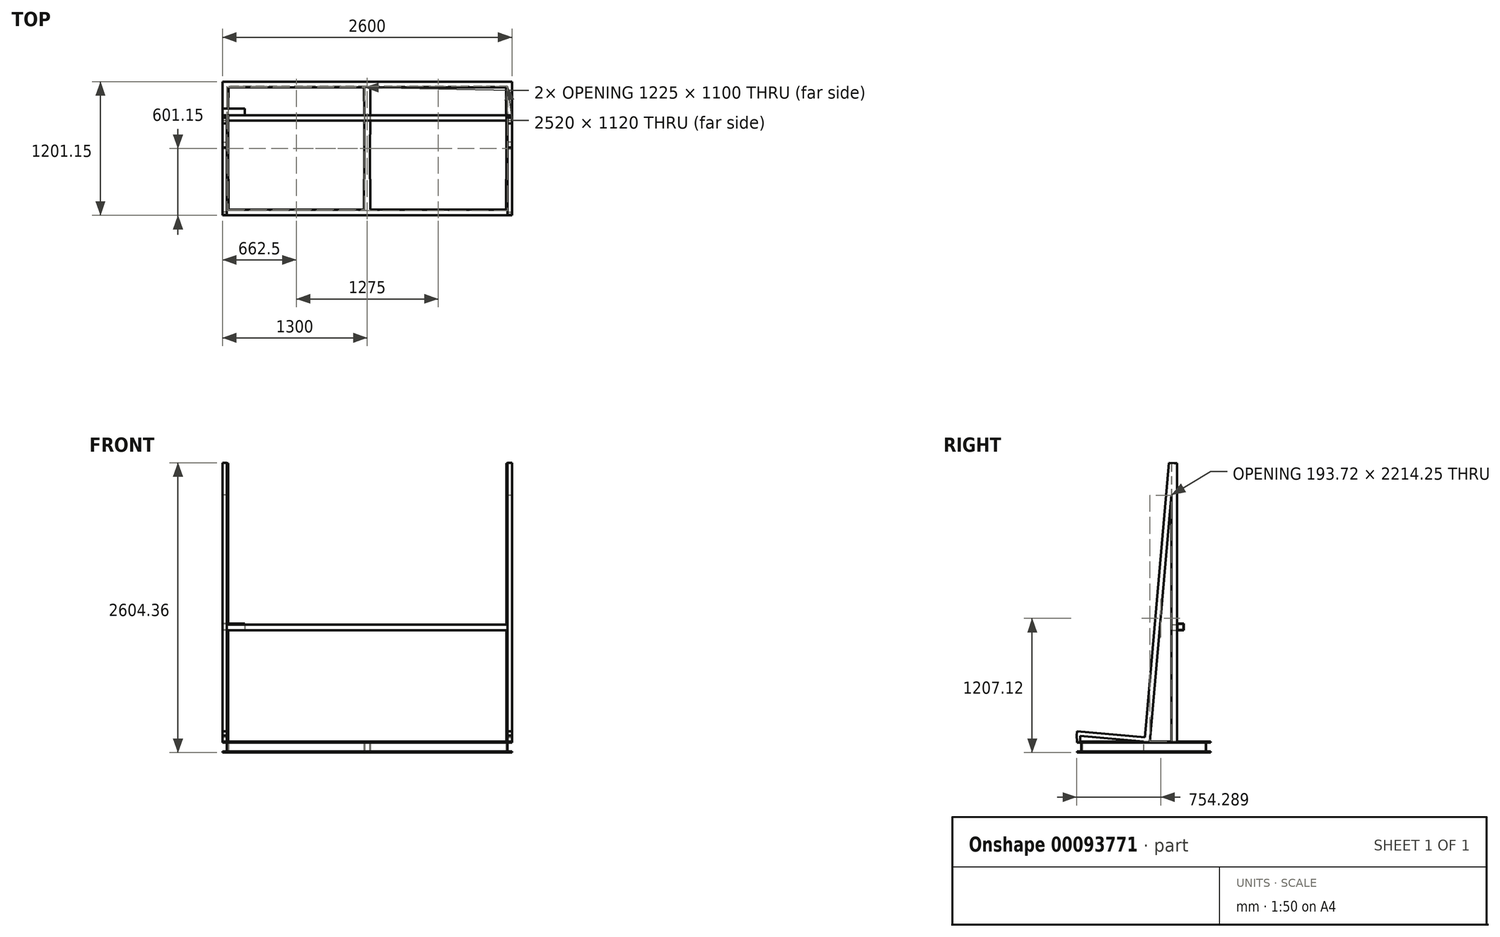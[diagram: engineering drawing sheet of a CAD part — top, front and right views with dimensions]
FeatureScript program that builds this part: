
annotation { "Feature Type Name" : "Feature", "Feature Type Description" : "" }
export const myFeature = defineFeature(function(context is Context, id is Id, definition is map)
    precondition{}
    {
        {
            var Q0;
            Q0=qCreatedBy(makeId("Top.planeOp"),FACE);
            var sketch = newSketch(context, id + "F0", { "sketchPlane" : qUnion([Q0])});
            skLineSegment(sketch, "E0.rect.bottom", {"start": v(1300, 600) * mm, "end": v(-1300, 600) * mm});
            skLineSegment(sketch, "E0.rect.top", {"start": v(1300, -600) * mm, "end": v(-1300, -600) * mm});
            skLineSegment(sketch, "E0.rect.left", {"start": v(1300, 600) * mm, "end": v(1300, -600) * mm});
            skLineSegment(sketch, "E0.rect.right", {"start": v(-1300, 600) * mm, "end": v(-1300, -600) * mm});
            skPoint(sketch, "E0.rect.middle", {"position": v(0, 0) * mm});
            skLineSegment(sketch, "E1.rect.bottom", {"start": v(1246.86, 550) * mm, "end": v(21.86, 550) * mm});
            skLineSegment(sketch, "E1.rect.top", {"start": v(1253.14, -550) * mm, "end": v(28.14, -550) * mm});
            skLineSegment(sketch, "E1.rect.left", {"start": v(1246.86, 550) * mm, "end": v(1253.14, -550) * mm});
            skLineSegment(sketch, "E1.rect.right", {"start": v(-1253.14, 550) * mm, "end": v(-1246.86, -550) * mm});
            skLineSegment(sketch, "E2.rect.left", {"start": v(21.86, 550) * mm, "end": v(28.14, -550) * mm});
            skLineSegment(sketch, "E2.rect.right", {"start": v(-28.14, 550) * mm, "end": v(-21.86, -550) * mm});
            skLineSegment(sketch, "E3.trimOffspring", {"start": v(-28.14, 550) * mm, "end": v(-1253.14, 550) * mm});
            skLineSegment(sketch, "E4.trimOffspring", {"start": v(-21.86, -550) * mm, "end": v(-1246.86, -550) * mm});
            skSolve(sketch);
        }
        {
            var Q0;
            Q0=makeQuery(id+"F0.imprint","IMPRINT",FACE,{"disambiguationData":[TD([[makeQuery(id+"F0.imprint","IMPRINT",EDGE,{"derivedFrom":sQuery(id+"F0.wireOp",EDGE,"E0.rect.bottom")}),1.0]])]});
            extrude(context, id + "F1", {"entities" : qUnion([Q0]), "depth" : 100 * mm});
        }
        {
            var Q0;
            Q0=makeQuery(id+"F1.opExtrude","SWEPT_FACE",FACE,{"disambiguationData":[OSD([sQuery(id+"F0.wireOp",EDGE,"E0.rect.right")])]});
            var sketch = newSketch(context, id + "F2", { "sketchPlane" : qUnion([Q0])});
            skLineSegment(sketch, "E5.bottom", {"start": v(-600, 90) * mm, "end": v(-560, 90) * mm});
            skLineSegment(sketch, "E5.top", {"start": v(-600, 10) * mm, "end": v(-560, 10) * mm});
            skLineSegment(sketch, "E5.left", {"start": v(-600, 90) * mm, "end": v(-600, 10) * mm});
            skLineSegment(sketch, "E5.right", {"start": v(-560, 90) * mm, "end": v(-560, 10) * mm});
            skLineSegment(sketch, "E6.bottom", {"start": v(600, 90) * mm, "end": v(560, 90) * mm});
            skLineSegment(sketch, "E6.top", {"start": v(600, 10) * mm, "end": v(560, 10) * mm});
            skLineSegment(sketch, "E6.left", {"start": v(600, 90) * mm, "end": v(600, 10) * mm});
            skLineSegment(sketch, "E6.right", {"start": v(560, 90) * mm, "end": v(560, 10) * mm});
            skSolve(sketch);
        }
        {
            var Q0;
            Q0=makeQuery(id+"F2.imprint","IMPRINT",FACE,{"disambiguationData":[TD([[makeQuery(id+"F2.imprint","IMPRINT",EDGE,{"derivedFrom":sQuery(id+"F2.wireOp",EDGE,"E5.bottom")}),-1.0]])]});
            var Q1;
            Q1=makeQuery(id+"F2.imprint","IMPRINT",FACE,{"disambiguationData":[TD([[makeQuery(id+"F2.imprint","IMPRINT",EDGE,{"derivedFrom":sQuery(id+"F2.wireOp",EDGE,"E6.bottom")}),1.0]])]});
            extrude(context, id + "F3", {"entities" : qUnion([Q0, Q1]), "operationType" : NewBodyOperationType.REMOVE, "endBound" : BoundingType.THROUGH_ALL, "oppositeDirection" : true, "depth" : 25 * mm});
        }
        {
            var Q0;
            Q0=makeQuery(id+"F3.boolean.opBoolean","COPY",FACE,{"derivedFrom":makeQuery(id+"F3.opExtrude","SWEPT_FACE",FACE,{"disambiguationData":[OSD([sQuery(id+"F2.wireOp",EDGE,"E6.right")])]})});
            var sketch = newSketch(context, id + "F4", { "sketchPlane" : qUnion([Q0])});
            skLineSegment(sketch, "E7.bottom", {"start": v(1300, 90) * mm, "end": v(1260, 90) * mm});
            skLineSegment(sketch, "E7.top", {"start": v(1300, 10) * mm, "end": v(1260, 10) * mm});
            skLineSegment(sketch, "E7.left", {"start": v(1300, 90) * mm, "end": v(1300, 10) * mm});
            skLineSegment(sketch, "E7.right", {"start": v(1260, 90) * mm, "end": v(1260, 10) * mm});
            skLineSegment(sketch, "E8.bottom", {"start": v(-1300, 90) * mm, "end": v(-1260, 90) * mm});
            skLineSegment(sketch, "E8.top", {"start": v(-1300, 10) * mm, "end": v(-1260, 10) * mm});
            skLineSegment(sketch, "E8.left", {"start": v(-1300, 90) * mm, "end": v(-1300, 10) * mm});
            skLineSegment(sketch, "E8.right", {"start": v(-1260, 90) * mm, "end": v(-1260, 10) * mm});
            skSolve(sketch);
        }
        {
            var Q0;
            Q0=makeQuery(id+"F4.imprint","IMPRINT",FACE,{"disambiguationData":[TD([[makeQuery(id+"F4.imprint","IMPRINT",EDGE,{"derivedFrom":sQuery(id+"F4.wireOp",EDGE,"E7.bottom")}),1.0]])]});
            var Q1;
            Q1=makeQuery(id+"F4.imprint","IMPRINT",FACE,{"disambiguationData":[TD([[makeQuery(id+"F4.imprint","IMPRINT",EDGE,{"derivedFrom":sQuery(id+"F4.wireOp",EDGE,"E8.bottom")}),1.0]])]});
            extrude(context, id + "F5", {"entities" : qUnion([Q0, Q1]), "operationType" : NewBodyOperationType.REMOVE, "endBound" : BoundingType.THROUGH_ALL, "oppositeDirection" : true, "depth" : 25 * mm});
        }
        {
            var Q0;
            Q0=qCreatedBy(makeId("Front.planeOp"),FACE);
            var sketch = newSketch(context, id + "F6", { "sketchPlane" : qUnion([Q0])});
            skLineSegment(sketch, "E9.bottom", {"start": v(0, 10) * mm, "end": v(-90, 10) * mm});
            skLineSegment(sketch, "E9.top", {"start": v(0, 90) * mm, "end": v(-90, 90) * mm});
            skLineSegment(sketch, "E9.left", {"start": v(0, 10) * mm, "end": v(0, 90) * mm});
            skLineSegment(sketch, "E9.right", {"start": v(-90, 10) * mm, "end": v(-90, 90) * mm});
            skSolve(sketch);
        }
        {
            var Q0;
            Q0=qSketchRegion(id+"F6",true);
            var Q1;
            Q1=makeQuery(id+"F1.opExtrude","SWEPT_FACE",FACE,{"disambiguationData":[OSD([sQuery(id+"F0.wireOp",EDGE,"E3.trimOffspring")])]});
            var Q2;
            Q2=makeQuery(id+"F1.opExtrude","SWEPT_FACE",FACE,{"disambiguationData":[OSD([sQuery(id+"F0.wireOp",EDGE,"E4.trimOffspring")])]});
            extrude(context, id + "F7", {"entities" : qUnion([Q0]), "operationType" : NewBodyOperationType.REMOVE, "endBound" : BoundingType.UP_TO_SURFACE, "oppositeDirection" : true, "endBoundEntityFace" : qUnion([Q1]), "depth" : 25 * mm, "hasSecondDirection" : true, "secondDirectionBound" : SecondDirectionBoundingType.UP_TO_SURFACE, "secondDirectionOppositeDirection" : false, "secondDirectionBoundEntityFace" : qUnion([Q2]), "secondDirectionDepth" : 25 * mm});
        }
        {
            var Q0;
            Q0=makeQuery(id+"F1.opExtrude","CAP_FACE",FACE,{"disambiguationData":[OSD([sQuery(id+"F0.wireOp",EDGE,"E0.rect.bottom"),sQuery(id+"F0.wireOp",EDGE,"E0.rect.top"),sQuery(id+"F0.wireOp",EDGE,"E0.rect.left"),sQuery(id+"F0.wireOp",EDGE,"E0.rect.right"),sQuery(id+"F0.wireOp",EDGE,"E1.rect.bottom"),sQuery(id+"F0.wireOp",EDGE,"E1.rect.top"),sQuery(id+"F0.wireOp",EDGE,"E1.rect.left"),sQuery(id+"F0.wireOp",EDGE,"E1.rect.right"),sQuery(id+"F0.wireOp",EDGE,"E2.rect.left"),sQuery(id+"F0.wireOp",EDGE,"E2.rect.right"),sQuery(id+"F0.wireOp",EDGE,"E3.trimOffspring"),sQuery(id+"F0.wireOp",EDGE,"E4.trimOffspring")])],"isStart":false});
            var sketch = newSketch(context, id + "F8", { "sketchPlane" : qUnion([Q0])});
            skLineSegment(sketch, "E10.bottom", {"start": v(-1300, 300) * mm, "end": v(-1251.43, 300) * mm});
            skLineSegment(sketch, "E10.top", {"start": v(-1300, 250) * mm, "end": v(-1251.43, 250) * mm});
            skLineSegment(sketch, "E10.left", {"start": v(-1300, 300) * mm, "end": v(-1300, 250) * mm});
            skLineSegment(sketch, "E10.right", {"start": v(-1251.43, 300) * mm, "end": v(-1251.43, 250) * mm});
            skLineSegment(sketch, "E11.bottom", {"start": v(1300, 300) * mm, "end": v(1248.57, 300) * mm});
            skLineSegment(sketch, "E11.top", {"start": v(1300, 250) * mm, "end": v(1248.57, 250) * mm});
            skLineSegment(sketch, "E11.left", {"start": v(1300, 300) * mm, "end": v(1300, 250) * mm});
            skLineSegment(sketch, "E11.right", {"start": v(1248.57, 300) * mm, "end": v(1248.57, 250) * mm});
            skSolve(sketch);
        }
        {
            var Q0;
            Q0 = qSketchRegion(id + "F8", true);
            extrude(context, id + "F9", {"entities" : qUnion([Q0]), "operationType" : NewBodyOperationType.ADD, "depth" : 2500 * mm});
        }
        {
            var Q0;
            {var subQ1=sQuery(id+"F0.wireOp",EDGE,"E0.rect.right");Q0=makeQuery(id+"F9.boolean.opBoolean","MERGE",FACE,{"derivedFrom":[makeQuery(id+"F5.boolean.opBoolean","SPLIT",FACE,{"disambiguationData":[TD([makeQuery(id+"F3.boolean.opBoolean","COPY",FACE,{"derivedFrom":makeQuery(id+"F3.opExtrude","SWEPT_FACE",FACE,{"disambiguationData":[OSD([sQuery(id+"F2.wireOp",EDGE,"E5.bottom")])]})})])],"derivedFrom":makeQuery(id+"F1.opExtrude","SWEPT_FACE",FACE,{"disambiguationData":[OSD([subQ1])]})}),makeQuery(id+"F9.opExtrude","SWEPT_FACE",FACE,{"disambiguationData":[OSD([sQuery(id+"F8.wireOp",EDGE,"E10.left")])]})]});}
            var sketch = newSketch(context, id + "F10", { "sketchPlane" : qUnion([Q0])});
            skLineSegment(sketch, "E12", {"start": v(-56.19, 98.98) * mm, "end": v(-275, 2600) * mm});
            skLineSegment(sketch, "E13", {"start": v(-275, 2600) * mm, "end": v(-225.2, 2604.36) * mm});
            skLineSegment(sketch, "E14", {"start": v(-225.2, 2604.36) * mm, "end": v(-6, 98.98) * mm});
            skLineSegment(sketch, "E15", {"start": v(-6, 98.98) * mm, "end": v(-56.19, 98.98) * mm});
            skLineSegment(sketch, "E16", {"start": v(-9.5, 139.09) * mm, "end": v(597.66, 192.2) * mm});
            skLineSegment(sketch, "E17", {"start": v(597.66, 192.2) * mm, "end": v(601.15, 152.36) * mm});
            skLineSegment(sketch, "E18", {"start": v(601.15, 152.36) * mm, "end": v(-6.02, 99.24) * mm});
            skLineSegment(sketch, "E19", {"start": v(-6.02, 99.24) * mm, "end": v(-9.5, 139.09) * mm});
            skLineSegment(sketch, "E20", {"start": v(600, 100) * mm, "end": v(601.15, 152.36) * mm});
            skLineSegment(sketch, "E21", {"start": v(600, 100) * mm, "end": v(570.03, 100) * mm});
            skLineSegment(sketch, "E22", {"start": v(570.03, 100) * mm, "end": v(570.03, 149.64) * mm});
            skSolve(sketch);
        }
        {
            var Q0;
            {var subQ0=sQuery(id+"F10.wireOp",EDGE,"E15");Q0=makeQuery(id+"F10.imprint","IMPRINT",FACE,{"disambiguationData":[TD([[makeQuery(id+"F10.imprint","IMPRINT",EDGE,{"derivedFrom":subQ0}),-1.0]])]});}
            var Q1;
            {var subQ12=sQuery(id+"F10.wireOp",EDGE,"E13");Q1=makeQuery(id+"F10.imprint","IMPRINT",FACE,{"disambiguationData":[TD([[makeQuery(id+"F10.imprint","IMPRINT",EDGE,{"derivedFrom":subQ12}),-1.0]])]});}
            var Q2;
            {var subQ2=sQuery(id+"F10.wireOp",EDGE,"E16");Q2=makeQuery(id+"F10.imprint","IMPRINT",FACE,{"disambiguationData":[TD([[makeQuery(id+"F10.imprint","IMPRINT",EDGE,{"derivedFrom":subQ2}),-1.0]])]});}
            var Q3;
            {var subQ0=sQuery(id+"F10.wireOp",EDGE,"E20");Q3=makeQuery(id+"F10.imprint","IMPRINT",FACE,{"disambiguationData":[TD([[makeQuery(id+"F10.imprint","IMPRINT",EDGE,{"derivedFrom":subQ0}),1.0]])]});}
            extrude(context, id + "F11", {"entities" : qUnion([Q0, Q1, Q2, Q3]), "operationType" : NewBodyOperationType.ADD, "oppositeDirection" : true, "depth" : 40 * mm});
        }
        {
            var Q0;
            Q0=makeQuery(id+"F11.opExtrude","SWEPT_BODY",BODY,{"disambiguationData":[OSD([sQuery(id+"F10.wireOp",EDGE,"E12"),sQuery(id+"F10.wireOp",EDGE,"E13"),sQuery(id+"F10.wireOp",EDGE,"E14"),sQuery(id+"F10.wireOp",EDGE,"E15")])]});
            var Q1;
            Q1=makeQuery(id+"F1.opExtrude","SWEPT_BODY",BODY,{"disambiguationData":[OSD([sQuery(id+"F0.wireOp",EDGE,"E0.rect.bottom"),sQuery(id+"F0.wireOp",EDGE,"E0.rect.top"),sQuery(id+"F0.wireOp",EDGE,"E0.rect.left"),sQuery(id+"F0.wireOp",EDGE,"E0.rect.right"),sQuery(id+"F0.wireOp",EDGE,"E1.rect.bottom"),sQuery(id+"F0.wireOp",EDGE,"E1.rect.top"),sQuery(id+"F0.wireOp",EDGE,"E1.rect.left"),sQuery(id+"F0.wireOp",EDGE,"E1.rect.right"),sQuery(id+"F0.wireOp",EDGE,"E2.rect.left"),sQuery(id+"F0.wireOp",EDGE,"E2.rect.right"),sQuery(id+"F0.wireOp",EDGE,"E3.trimOffspring"),sQuery(id+"F0.wireOp",EDGE,"E4.trimOffspring")])]});
            var Q2;
            Q2=qCreatedBy(makeId("Right.planeOp"),FACE);
            mirror(context, id + "F12", {"operationType" : NewBodyOperationType.ADD, "entities" : qUnion([Q0, Q1]), "mirrorPlane" : qUnion([Q2])});
        }
        {
            var Q0;
            Q0=makeQuery(id+"F12.opPattern","COPY",FACE,{"derivedFrom":makeQuery(id+"F9.opExtrude","SWEPT_FACE",FACE,{"disambiguationData":[OSD([sQuery(id+"F8.wireOp",EDGE,"E11.right")])]}),"instanceName":"1"});
            var sketch = newSketch(context, id + "F13", { "sketchPlane" : qUnion([Q0])});
            skLineSegment(sketch, "E23.bottom", {"start": v(250, 1150) * mm, "end": v(300, 1150) * mm});
            skLineSegment(sketch, "E23.top", {"start": v(250, 1100) * mm, "end": v(300, 1100) * mm});
            skLineSegment(sketch, "E23.left", {"start": v(250, 1150) * mm, "end": v(250, 1100) * mm});
            skLineSegment(sketch, "E23.right", {"start": v(300, 1150) * mm, "end": v(300, 1100) * mm});
            skSolve(sketch);
        }
        {
            var Q0;
            Q0=makeQuery(id+"F13.imprint","IMPRINT",FACE,{"disambiguationData":[TD([[makeQuery(id+"F13.imprint","IMPRINT",EDGE,{"derivedFrom":sQuery(id+"F13.wireOp",EDGE,"E23.bottom")}),-1.0]])]});
            extrude(context, id + "F14", {"entities" : qUnion([Q0]), "operationType" : NewBodyOperationType.ADD, "endBound" : BoundingType.UP_TO_NEXT, "depth" : 25 * mm});
        }
        {
            var Q0;
            {var subQ0=sQuery(id+"F8.wireOp",EDGE,"E10.left");var subQ1=sQuery(id+"F0.wireOp",EDGE,"E0.rect.right");Q0=makeQuery(id+"F11.boolean.opBoolean","MERGE",FACE,{"derivedFrom":[makeQuery(id+"F9.boolean.opBoolean","MERGE",FACE,{"derivedFrom":[makeQuery(id+"F5.boolean.opBoolean","SPLIT",FACE,{"disambiguationData":[TD([makeQuery(id+"F3.boolean.opBoolean","COPY",FACE,{"derivedFrom":makeQuery(id+"F3.opExtrude","SWEPT_FACE",FACE,{"disambiguationData":[OSD([sQuery(id+"F2.wireOp",EDGE,"E5.bottom")])]})})])],"derivedFrom":makeQuery(id+"F1.opExtrude","SWEPT_FACE",FACE,{"disambiguationData":[OSD([subQ1])]})}),makeQuery(id+"F9.opExtrude","SWEPT_FACE",FACE,{"disambiguationData":[OSD([subQ0])]})]}),makeQuery(id+"F11.opExtrude","CAP_FACE",FACE,{"disambiguationData":[OSD([subQ1,sQuery(id+"F8.wireOp",EDGE,"E10.top"),subQ0,sQuery(id+"F10.wireOp",EDGE,"E12"),sQuery(id+"F10.wireOp",EDGE,"E13"),sQuery(id+"F10.wireOp",EDGE,"E14"),sQuery(id+"F10.wireOp",EDGE,"E15"),sQuery(id+"F10.wireOp",EDGE,"E16"),sQuery(id+"F10.wireOp",EDGE,"E17"),sQuery(id+"F10.wireOp",EDGE,"E18"),sQuery(id+"F10.wireOp",EDGE,"E19"),sQuery(id+"F10.wireOp",EDGE,"E20"),sQuery(id+"F10.wireOp",EDGE,"E21"),sQuery(id+"F10.wireOp",EDGE,"E22")])],"isStart":true})]});}
            var sketch = newSketch(context, id + "F15", { "sketchPlane" : qUnion([Q0])});
            skLineSegment(sketch, "E24.bottom", {"start": v(-300, 1160) * mm, "end": v(-360, 1160) * mm});
            skLineSegment(sketch, "E24.top", {"start": v(-300, 1100) * mm, "end": v(-360, 1100) * mm});
            skLineSegment(sketch, "E24.left", {"start": v(-300, 1160) * mm, "end": v(-300, 1100) * mm});
            skLineSegment(sketch, "E24.right", {"start": v(-360, 1160) * mm, "end": v(-360, 1100) * mm});
            skLineSegment(sketch, "E25.bottom", {"start": v(-357.5, 1157.5) * mm, "end": v(-302.5, 1157.5) * mm});
            skLineSegment(sketch, "E25.top", {"start": v(-357.5, 1102.5) * mm, "end": v(-302.5, 1102.5) * mm});
            skLineSegment(sketch, "E25.left", {"start": v(-357.5, 1157.5) * mm, "end": v(-357.5, 1102.5) * mm});
            skLineSegment(sketch, "E25.right", {"start": v(-302.5, 1157.5) * mm, "end": v(-302.5, 1102.5) * mm});
            skSolve(sketch);
        }
        {
            var Q0;
            Q0=makeQuery(id+"F15.imprint","IMPRINT",FACE,{"disambiguationData":[TD([[makeQuery(id+"F15.imprint","IMPRINT",EDGE,{"derivedFrom":sQuery(id+"F15.wireOp",EDGE,"E24.bottom")}),1.0]])]});
            extrude(context, id + "F16", {"entities" : qUnion([Q0]), "operationType" : NewBodyOperationType.ADD, "oppositeDirection" : true, "depth" : 200 * mm});
        }
    });
